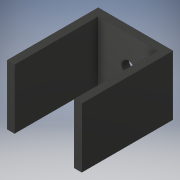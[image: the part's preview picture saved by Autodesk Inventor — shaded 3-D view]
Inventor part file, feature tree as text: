
AUTODESK INVENTOR PART (.ipt)
format: ipt  version: 2019.4 (Build 234330000, 330)  size: 105,984 bytes
history: native  units: mm
features: extrude x2, sketch x1, hole x1
ambient origin geometry x8: Origin, YZ Plane, XZ Plane, XY Plane, X Axis, Y Axis, Z Axis, Center Point
bodies: Solid1 (feature_tree)
feature tree (4):
  sketch  "Sketch1"  dims[d0=25.0mm d1=20.0mm d2=2.5mm d3=2.5mm d4=2.5mm d5=0.0mm d6=30.5mm d7=0.0mm d8=4.5mm d9=6.0mm d10=4.0mm d11=2.0mm d12=90.0deg d13=8.0mm d14=20.594885mm]
  extrude  "Extrusion1"  Depth=20.0mm
  extrude  "Extrusion2"  Depth=2.5mm
  hole  "Hole1"  [1 undecoded]
note: 1 required parameter value undecoded (feature->parameter linkage not recoverable at this tier; creation-order binding heuristic only, values carry confidence <= 0.55)
